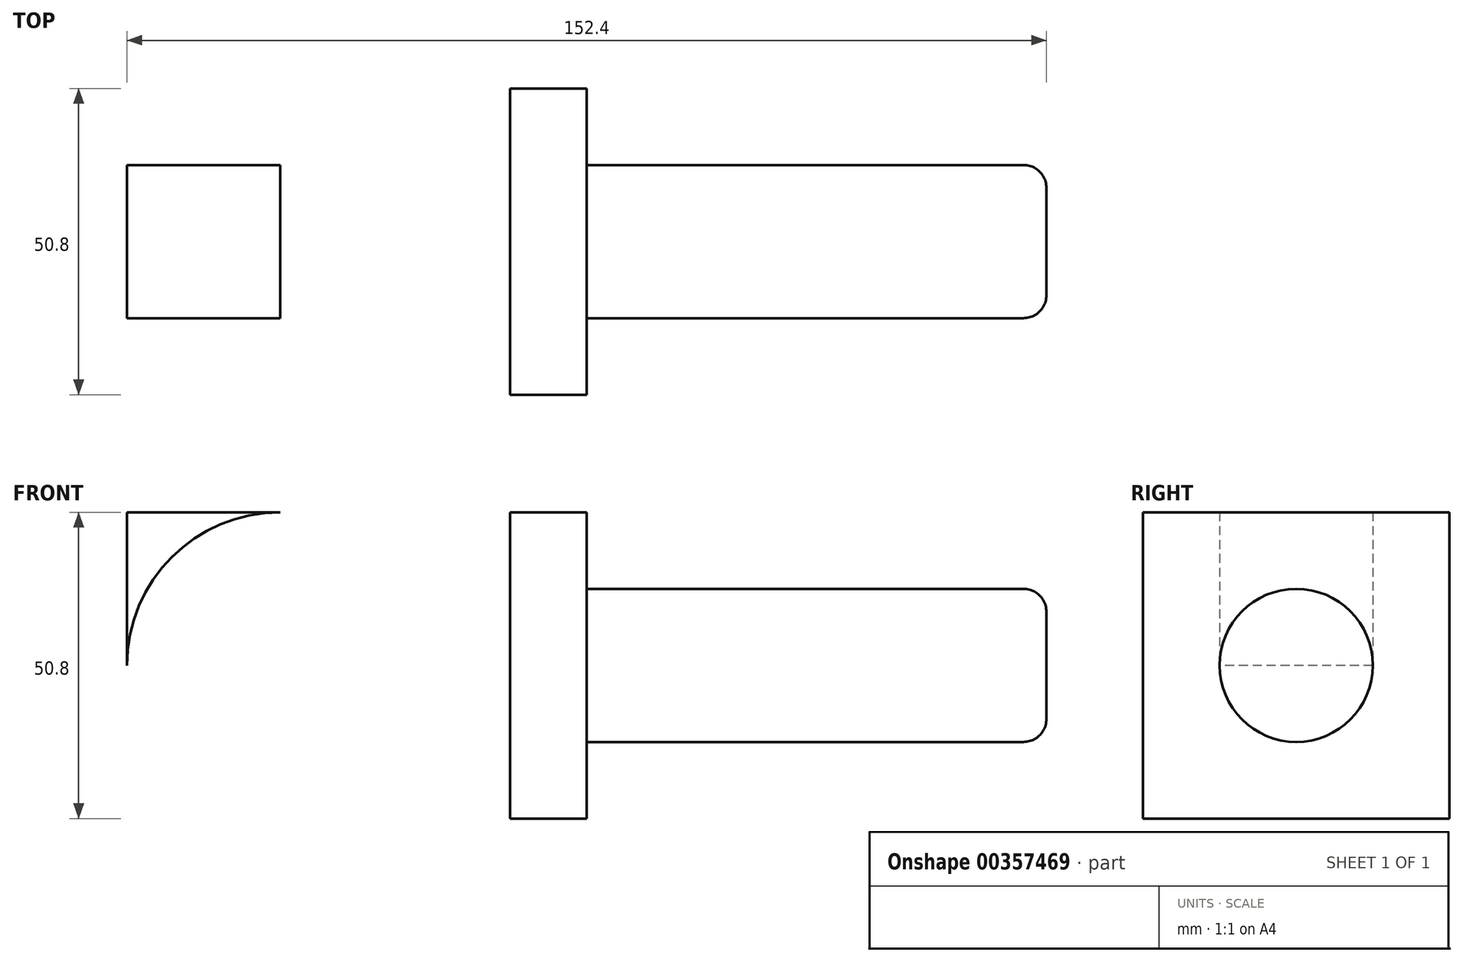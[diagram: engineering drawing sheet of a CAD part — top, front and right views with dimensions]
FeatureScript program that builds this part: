
annotation { "Feature Type Name" : "Feature", "Feature Type Description" : "" }
export const myFeature = defineFeature(function(context is Context, id is Id, definition is map)
    precondition{}
    {
        {
            var Q0;
            Q0=qCreatedBy(makeId("Right.planeOp"),FACE);
            var sketch = newSketch(context, id + "F0", { "sketchPlane" : qUnion([Q0])});
            skCircle(sketch, "E0", {"center": v(0, 0) * mm, "radius": 12.7 * mm});
            skSolve(sketch);
        }
        {
            var Q0;
            Q0=makeQuery(id+"F0.imprint","IMPRINT",FACE,{"disambiguationData":[TD([[makeQuery(id+"F0.imprint","IMPRINT",EDGE,{"derivedFrom":sQuery(id+"F0.wireOp",EDGE,"E0")}),1.0]])]});
            extrude(context, id + "F1", {"entities" : qUnion([Q0]), "depth" : 76.2 * mm});
        }
        {
            var Q0;
            Q0=qCreatedBy(makeId("Front.planeOp"),FACE);
            var sketch = newSketch(context, id + "F2", { "sketchPlane" : qUnion([Q0])});
            skLineSegment(sketch, "E1", {"start": v(0, 0) * mm, "end": v(0, 25.4) * mm});
            skLineSegment(sketch, "E2", {"start": v(0, 25.4) * mm, "end": v(-12.7, 25.4) * mm});
            skLineSegment(sketch, "E3", {"start": v(-12.7, 25.4) * mm, "end": v(-12.7, -25.4) * mm});
            skLineSegment(sketch, "E4", {"start": v(-12.7, -25.4) * mm, "end": v(0, -25.4) * mm});
            skLineSegment(sketch, "E5", {"start": v(0, -25.4) * mm, "end": v(0, 25.4) * mm});
            skSolve(sketch);
        }
        {
            var Q0;
            {var subQ0=sQuery(id+"F2.wireOp",EDGE,"E2");Q0=makeQuery(id+"F2.imprint","IMPRINT",FACE,{"disambiguationData":[TD([[makeQuery(id+"F2.imprint","IMPRINT",EDGE,{"derivedFrom":subQ0}),1.0]])]});}
            extrude(context, id + "F3", {"entities" : qUnion([Q0]), "operationType" : NewBodyOperationType.ADD, "endBound" : BoundingType.SYMMETRIC, "depth" : 50.8 * mm});
        }
        {
            var Q0;
            Q0=makeQuery(id+"F3.opExtrude","SWEPT_FACE",FACE,{"disambiguationData":[OSD([sQuery(id+"F2.wireOp",EDGE,"E3")])]});
            var sketch = newSketch(context, id + "F4", { "sketchPlane" : qUnion([Q0])});
            skLineSegment(sketch, "E6", {"start": v(0, 44.15) * mm, "end": v(0, -39.9) * mm, "construction": true});
            skLineSegment(sketch, "E7.right", {"start": v(-12.7, 25.4) * mm, "end": v(-12.7, -25.4) * mm});
            skLineSegment(sketch, "E8.MirrorCS", {"start": v(12.7, 25.4) * mm, "end": v(12.7, -25.4) * mm});
            skLineSegment(sketch, "E9", {"start": v(-12.7, 25.4) * mm, "end": v(12.7, 25.4) * mm});
            skLineSegment(sketch, "E10", {"start": v(-12.7, -25.4) * mm, "end": v(12.7, -25.4) * mm});
            skSolve(sketch);
        }
        {
            var Q0;
            Q0=makeQuery(id+"F4.imprint","IMPRINT",FACE,{"disambiguationData":[TD([[makeQuery(id+"F4.imprint","IMPRINT",EDGE,{"derivedFrom":sQuery(id+"F4.wireOp",EDGE,"E7.right")}),1.0]])]});
            extrude(context, id + "F5", {"entities" : qUnion([Q0]), "operationType" : NewBodyOperationType.ADD, "depth" : 63.5 * mm});
        }
        {
            var Q0;
            Q0=makeQuery(id+"F5.opExtrude","SWEPT_FACE",FACE,{"disambiguationData":[OSD([sQuery(id+"F4.wireOp",EDGE,"E8.MirrorCS")])]});
            var sketch = newSketch(context, id + "F6", { "sketchPlane" : qUnion([Q0])});
            skCircle(sketch, "E11", {"center": v(-50.8, 0) * mm, "radius": 9.53 * mm});
            skArc(sketch, "E12", {"start": v(-76.2, 0) * mm, "mid": v(-68.76, 17.96) * mm, "end": v(-50.8, 25.4) * mm});
            skArc(sketch, "E13", {"start": v(-76.2, 0) * mm, "mid": v(-68.76, -17.96) * mm, "end": v(-50.8, -25.4) * mm});
            skSolve(sketch);
        }
        {
            var Q0;
            {var subQ0=sQuery(id+"F6.wireOp",EDGE,"E12");Q0=makeQuery(id+"F6.imprint","IMPRINT",FACE,{"disambiguationData":[TD([[makeQuery(id+"F6.imprint","IMPRINT",EDGE,{"derivedFrom":subQ0}),1.0]])]});}
            var Q1;
            {var subQ0=sQuery(id+"F6.wireOp",EDGE,"E13");Q1=makeQuery(id+"F6.imprint","IMPRINT",FACE,{"disambiguationData":[TD([[makeQuery(id+"F6.imprint","IMPRINT",EDGE,{"derivedFrom":subQ0}),-1.0]])]});}
            extrude(context, id + "F7", {"entities" : qUnion([Q0, Q1]), "operationType" : NewBodyOperationType.REMOVE, "endBound" : BoundingType.THROUGH_ALL, "oppositeDirection" : true, "depth" : 25.4 * mm});
        }
        {
            var Q0;
            Q0=makeQuery(id+"F6.imprint","IMPRINT",FACE,{"disambiguationData":[TD([[makeQuery(id+"F6.imprint","IMPRINT",EDGE,{"derivedFrom":sQuery(id+"F6.wireOp",EDGE,"E11")}),1.0]])]});
            extrude(context, id + "F8", {"entities" : qUnion([Q0]), "operationType" : NewBodyOperationType.REMOVE, "endBound" : BoundingType.THROUGH_ALL, "oppositeDirection" : true, "depth" : 25.4 * mm});
        }
        {
            var Q0;
            Q0=makeQuery(id+"F1.opExtrude","CAP_EDGE",EDGE,{"disambiguationData":[OSD([sQuery(id+"F0.wireOp",EDGE,"E0")])],"isStart":false});
            var Q1;
            Q1=makeQuery(id+"F1.opExtrude","CAP_EDGE",EDGE,{"disambiguationData":[OSD([sQuery(id+"F0.wireOp",EDGE,"E0")])],"isStart":true});
            fillet(context, id + "F9", {"entities" : qUnion([Q0, Q1]), "radius" : 3.8 * mm, "tangentPropagation" : true, "allowEdgeOverflow" : false});
        }
    });
